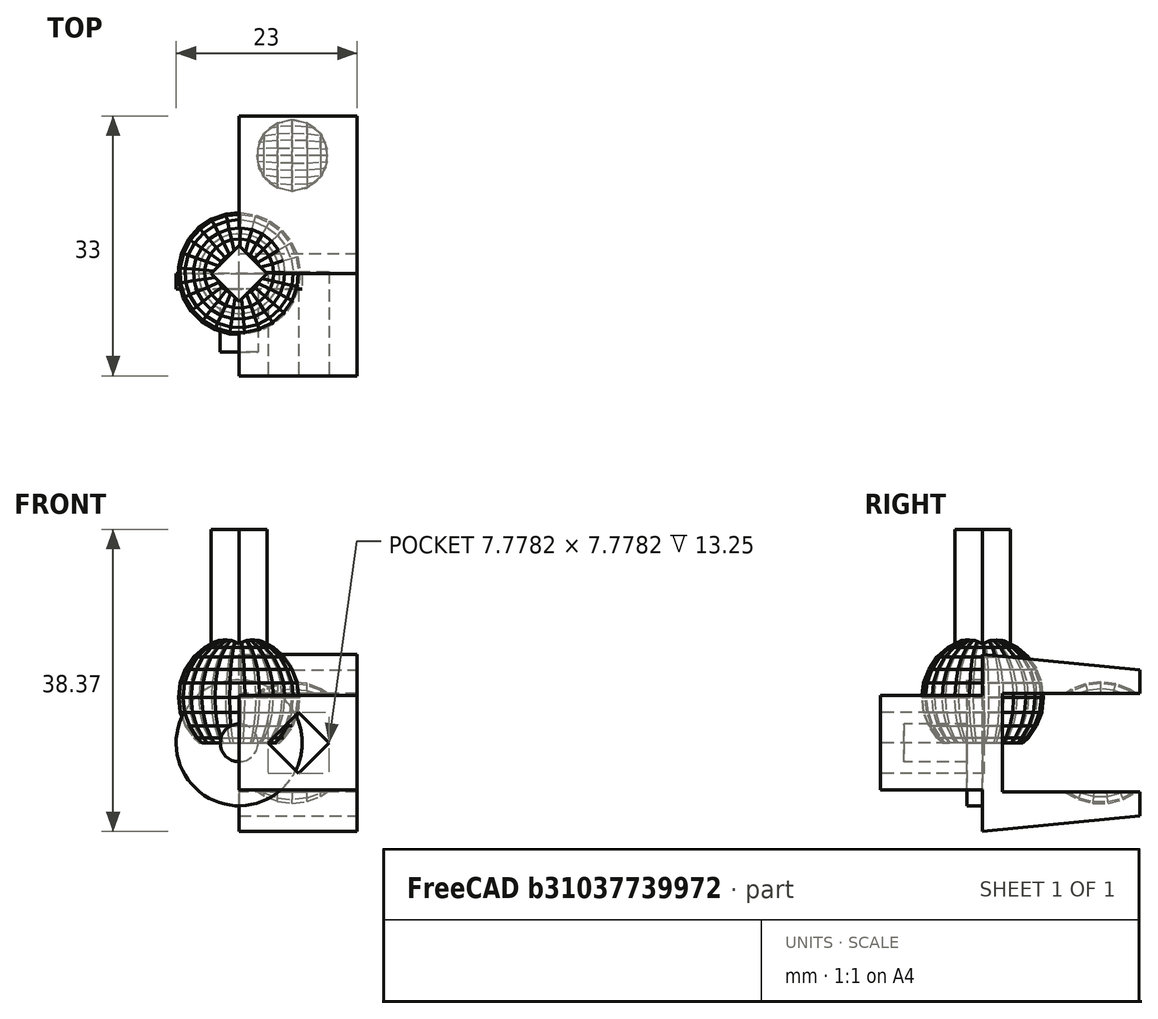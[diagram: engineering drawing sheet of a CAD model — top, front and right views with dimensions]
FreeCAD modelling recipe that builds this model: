
FCSTD DOCUMENT  (FreeCAD 0.15R4671 (Git))
Label: Clipper
License: All rights reserved
LicenseURL: http://es.wikipedia.org/wiki/Todos_los_derechos_reservados
objects: Part::Box×3, Part::MultiFuse×3, Part::Feature×2, Part::FeaturePython×2, Part::Cut×2, Part::Cylinder×2, Part::Wedge×1, Part::Mirroring×1, App::DocumentObjectGroup×1, Part::Offset×1
note: 17 computed .brp shape members not serialized (recipe doc carries the construction recipe); baked Part::Feature solids carry a one-line shape summary decoded from their .brp

FEATURE [Part::Wedge] Wedge002  label="WedgeBase"
  Placement = pos=(0,0,6.25) rot=(0,0,1;0rad)
  X2max = 15
  X2min = 0
  Xmax = 15
  Xmin = 0
  Ymax = 20
  Ymin = 0
  Z2max = 3
  Z2min = 0
  Zmax = 5
  Zmin = 0
FEATURE [Part::Mirroring] Part__Mirroring  label="Wedge"
  Base = (7.5,12.5,0)
  Normal = (0,0,1)
  Source = -> Wedge002
FEATURE [Part::Box] Box  label="ClipperBase"
  Height = 20
  Length = 15
  Placement = pos=(0,0,-10) rot=(0,0,1;0rad)
  Width = 2.5
FEATURE [Part::Feature] BallJoint001_solid001  label="Ball Joint"
  Placement = pos=(0,0,0) rot=(0,0,1;0.785398rad)
  shape: bbox 15.46 x 15.46 x 27.13 mm, 528 faces (baked)
FEATURE [Part::Feature] BallJoint001_solid001001  label="BallJoint001"
  Placement = pos=(12.5,15,0) rot=(0,-1,0;1.5708rad)
  shape: bbox 27.13 x 15.47 x 15.44 mm, 528 faces (baked)
FEATURE [Part::FeaturePython] Clone  label="Clone of WedgeBase"  # Draft clone (typed FeaturePython)
  Objects = -> [Wedge002]
  Placement = pos=(0,0,6.25) rot=(0,0,1;0rad)
  Scale = (1,1,1)
FEATURE [Part::MultiFuse] Fusion  label="Tong"
  Shapes = -> [Part__Mirroring,Clone,Box]
FEATURE [Part::Cut] Cut  label="Base Clipper"
  Base = -> Fusion
  Tool = -> BallJoint001_solid001001
FEATURE [Part::FeaturePython] Clone001  label="Clone of Base Clipper"  # Draft clone (typed FeaturePython)
  Objects = -> [Cut]
  Scale = (1,1,1)
FEATURE [App::DocumentObjectGroup] Group  label="Base"
  Group = -> [BallJoint001_solid001,Cut]
FEATURE [Part::Box] Box001  label="Socket"
  Height = 12
  Length = 15
  Placement = pos=(0,-13,-6) rot=(0,0,1;0rad)
  Width = 15
FEATURE [Part::MultiFuse] Fusion001  label="Stackable tong"
  Shapes = -> [Clone001,Box001]
FEATURE [Part::Box] Box002  label="Stick"
  Height = 5
  Length = 5
  Placement = pos=(4,-25,0) rot=(0,1,0;0.785398rad)
  Width = 25
FEATURE [Part::Offset] Offset
  Fill = false
  Intersection = false
  Join = 2
  Mode = 0
  SelfIntersection = false
  Source = -> Box002
  Value = 0.25
FEATURE [Part::Cut] Cut001  label="Stackable Clipper"
  Base = -> Fusion001
  Tool = -> Offset
FEATURE [Part::Cylinder] Cylinder  label="PivotStick"
  Angle = 360
  Height = 10
  Placement = pos=(0,0,0) rot=(1,0,0;1.5708rad)
  Radius = 2.4
FEATURE [Part::Cylinder] Cylinder001  label="RoundBase"
  Angle = 360
  Height = 2
  Placement = pos=(0,0,0) rot=(1,0,0;1.5708rad)
  Radius = 8
FEATURE [Part::MultiFuse] Fusion002  label="Pivot"
  Shapes = -> [Cylinder001,Cylinder]
